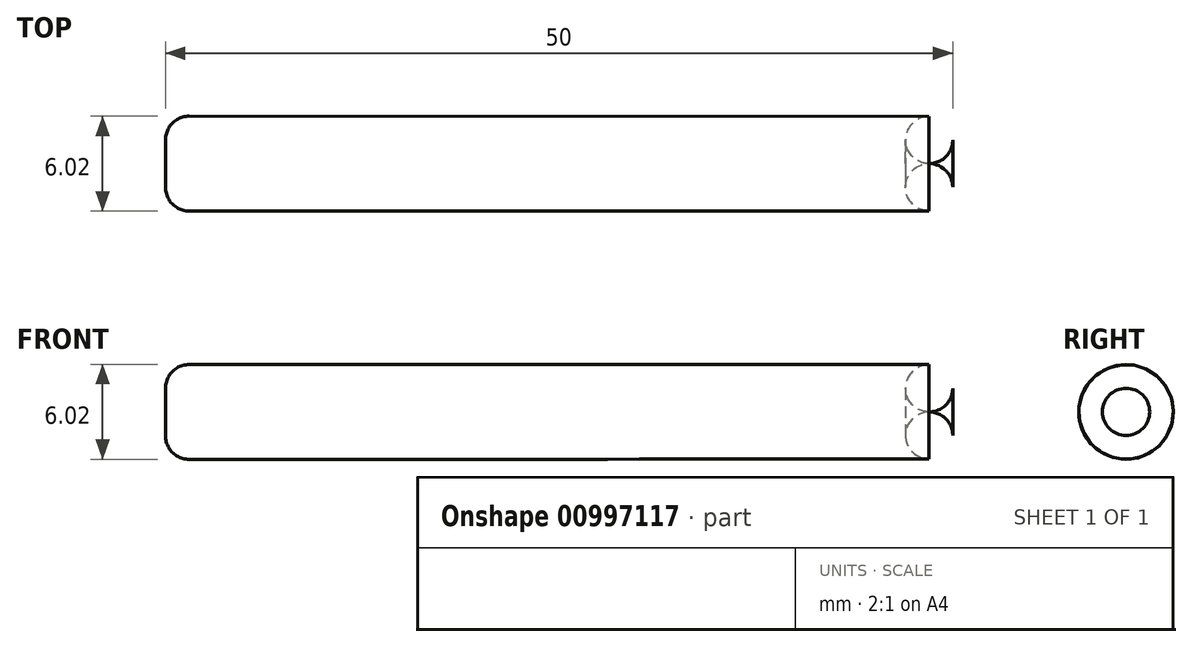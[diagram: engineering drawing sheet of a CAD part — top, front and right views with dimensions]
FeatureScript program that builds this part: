
annotation { "Feature Type Name" : "Feature", "Feature Type Description" : "" }
export const myFeature = defineFeature(function(context is Context, id is Id, definition is map)
    precondition{}
    {
        {
            var Q0;
            Q0=qCreatedBy(makeId("Front.planeOp"),FACE);
            var sketch = newSketch(context, id + "F0", { "sketchPlane" : qUnion([Q0])});
            skLineSegment(sketch, "E0.top", {"start": v(25.75, -1.5) * mm, "end": v(-24.25, -1.5) * mm});
            skPoint(sketch, "E0.middle", {"position": v(0, 0) * mm});
            skLineSegment(sketch, "E1", {"start": v(-24.25, -1.5) * mm, "end": v(-24.25, 0) * mm});
            skLineSegment(sketch, "E2", {"start": v(24.25, 1.5) * mm, "end": v(-22.75, 1.5) * mm});
            skArc(sketch, "E3", {"start": v(-22.75, 1.5) * mm, "mid": v(-23.81, 1.07) * mm, "end": v(-24.25, 0) * mm});
            skLineSegment(sketch, "E4", {"start": v(25.75, -1.5) * mm, "end": v(25.75, 0) * mm});
            skArc(sketch, "E5", {"start": v(25.75, 0) * mm, "mid": v(25.31, 1.06) * mm, "end": v(24.25, 1.5) * mm});
            skSolve(sketch);
        }
        {
            var Q0;
            Q0 = qSketchRegion(id + "F0", true);
            var Q1;
            Q1=sQuery(id+"F0.wireOp",EDGE,"E0.top");
            revolve(context, id + "F1", {"surfaceOperationType" : NewSurfaceOperationType.NEW, "entities" : qUnion([Q0]), "axis" : qUnion([Q1]), "revolveType" : RevolveType.FULL});
        }
    });
